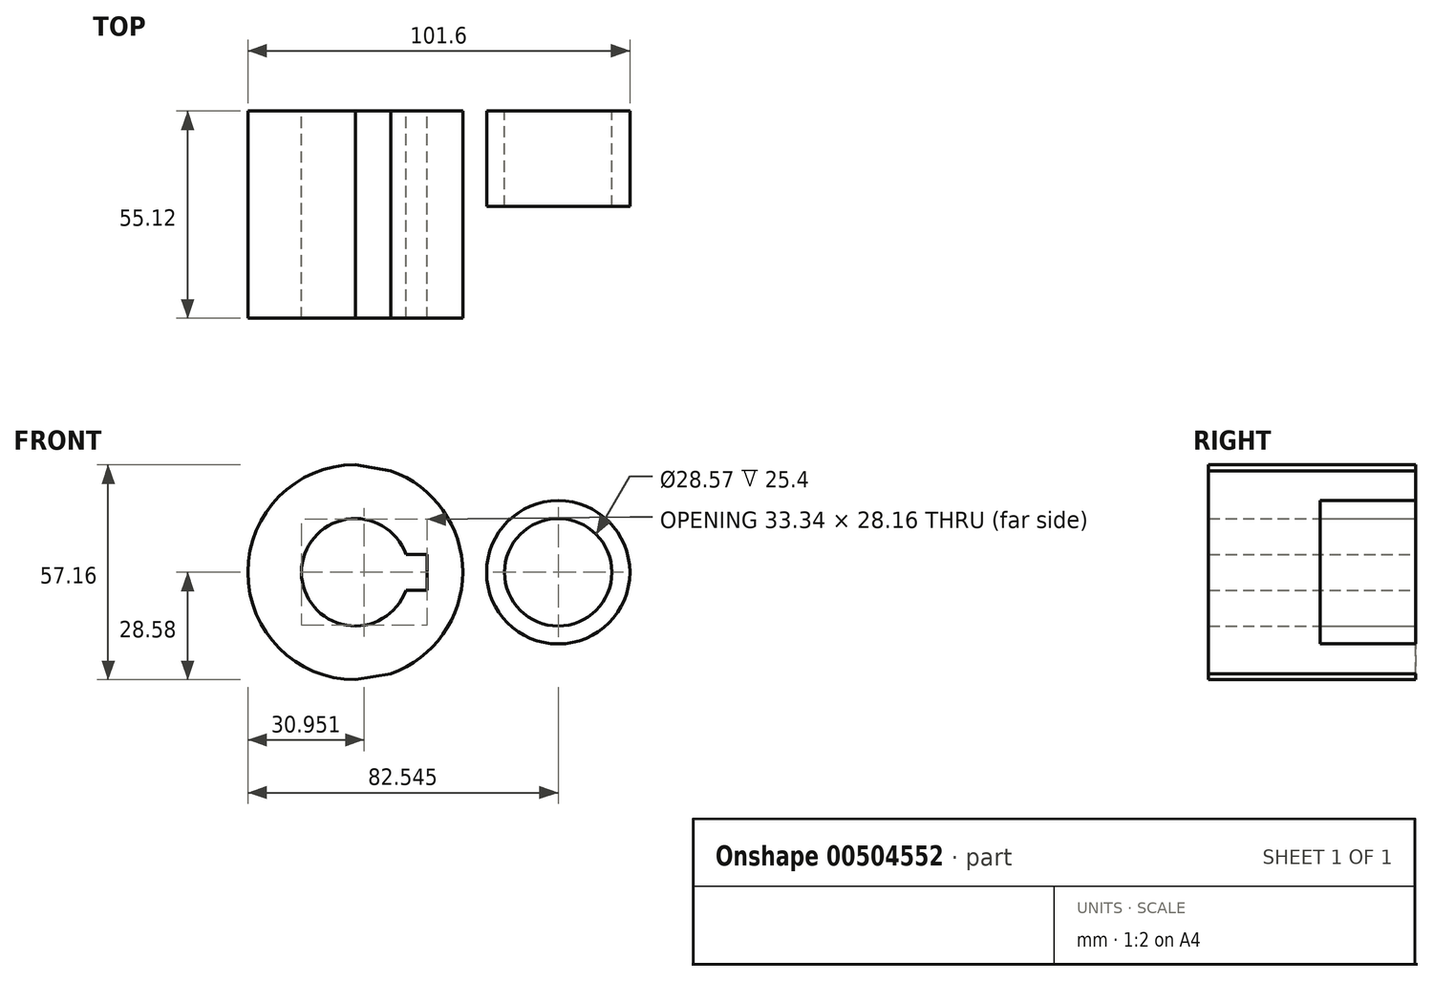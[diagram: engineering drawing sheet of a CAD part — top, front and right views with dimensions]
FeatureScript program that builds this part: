
annotation { "Feature Type Name" : "Feature", "Feature Type Description" : "" }
export const myFeature = defineFeature(function(context is Context, id is Id, definition is map)
    precondition{}
    {
        {
            var Q0;
            Q0=qCreatedBy(makeId("Front.planeOp"),FACE);
            var sketch = newSketch(context, id + "F0", { "sketchPlane" : qUnion([Q0])});
            skCircle(sketch, "E0", {"center": v(0, 0) * mm, "radius": 28.58 * mm});
            skCircle(sketch, "E1", {"center": v(53.98, 0) * mm, "radius": 19.05 * mm});
            skLineSegment(sketch, "E2", {"start": v(0, 28.57) * mm, "end": v(57.2, 18.78) * mm});
            skLineSegment(sketch, "E3", {"start": v(0, -28.57) * mm, "end": v(57.2, -18.78) * mm});
            skCircle(sketch, "E4", {"center": v(0, 0) * mm, "radius": 14.29 * mm});
            skCircle(sketch, "E5", {"center": v(53.98, 0) * mm, "radius": 14.29 * mm});
            skLineSegment(sketch, "E6.bottom", {"start": v(-19.05, 4.76) * mm, "end": v(19.05, 4.76) * mm});
            skLineSegment(sketch, "E6.top", {"start": v(-19.05, -4.76) * mm, "end": v(19.05, -4.76) * mm});
            skLineSegment(sketch, "E6.left", {"start": v(-19.05, 4.76) * mm, "end": v(-19.05, -4.76) * mm});
            skLineSegment(sketch, "E6.right", {"start": v(19.05, 4.76) * mm, "end": v(19.05, -4.76) * mm});
            skSolve(sketch);
        }
        {
            var Q0;
            {var subQ4=sQuery(id+"F0.wireOp",EDGE,"E6.left");Q0=makeQuery(id+"F0.imprint","IMPRINT",FACE,{"disambiguationData":[TD([[makeQuery(id+"F0.imprint","IMPRINT",EDGE,{"derivedFrom":subQ4}),-1.0]])]});}
            var Q1;
            Q1=makeQuery(id+"F0.imprint","IMPRINT",FACE,{"disambiguationData":[TD([[makeQuery(id+"F0.imprint","IMPRINT",EDGE,{"derivedFrom":sQuery(id+"F0.wireOp",EDGE,"E5")}),-1.0]])]});
            var Q2;
            {var subQ0=sQuery(id+"F0.wireOp",EDGE,"E2");var subQ1=sQuery(id+"F0.wireOp",EDGE,"E0");var subQ2=makeQuery(id+"F0.imprint","INTERSECT",VERTEX,{"disambiguationData":[OD(1.0)],"derivedFrom":[subQ1,subQ0]});Q2=makeQuery(id+"F0.imprint","IMPRINT",FACE,{"disambiguationData":[TD([[makeQuery(id+"F0.imprint","IMPRINT",EDGE,{"disambiguationData":[TD([[subQ2,1.0]])],"derivedFrom":subQ1}),-1.0]])]});}
            extrude(context, id + "F1", {"entities" : qUnion([Q0, Q1, Q2]), "depth" : 25.4 * mm});
        }
        {
            var Q0;
            {var subQ5=sQuery(id+"F0.wireOp",EDGE,"E6.left");Q0=makeQuery(id+"F0.imprint","IMPRINT",FACE,{"disambiguationData":[TD([[makeQuery(id+"F0.imprint","IMPRINT",EDGE,{"derivedFrom":subQ5}),1.0]])]});}
            extrude(context, id + "F2", {"entities" : qUnion([Q0]), "operationType" : NewBodyOperationType.ADD, "depth" : 25.4 * mm});
        }
        {
            var Q0;
            {var subQ4=sQuery(id+"F0.wireOp",EDGE,"E6.left");Q0=makeQuery(id+"F0.imprint","IMPRINT",FACE,{"disambiguationData":[TD([[makeQuery(id+"F0.imprint","IMPRINT",EDGE,{"derivedFrom":subQ4}),-1.0]])]});}
            var Q1;
            {var subQ5=sQuery(id+"F0.wireOp",EDGE,"E6.left");Q1=makeQuery(id+"F0.imprint","IMPRINT",FACE,{"disambiguationData":[TD([[makeQuery(id+"F0.imprint","IMPRINT",EDGE,{"derivedFrom":subQ5}),1.0]])]});}
            extrude(context, id + "F3", {"entities" : qUnion([Q0, Q1]), "operationType" : NewBodyOperationType.ADD, "depth" : 55.12 * mm});
        }
    });
